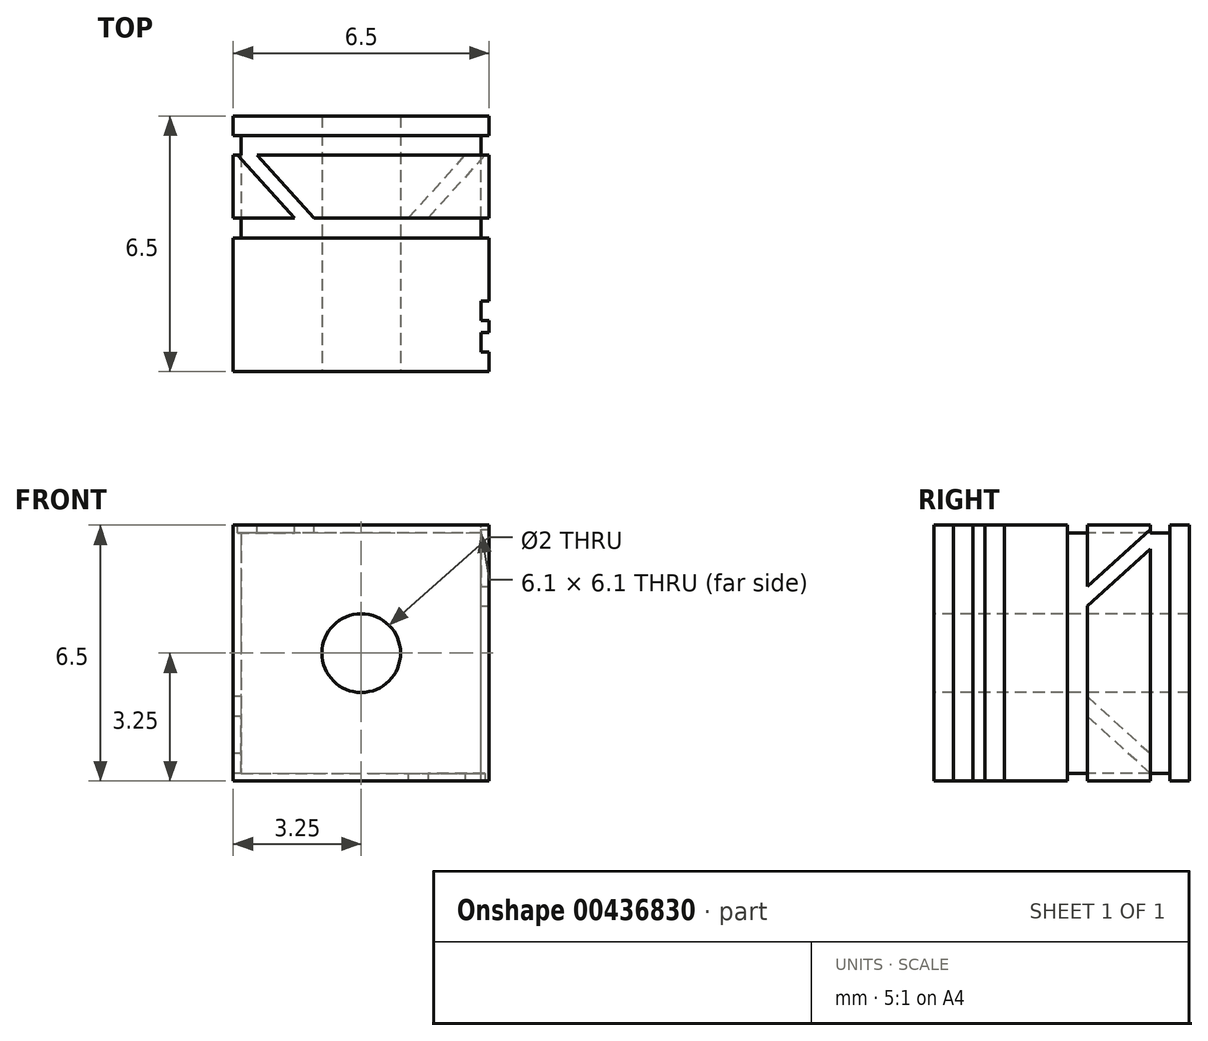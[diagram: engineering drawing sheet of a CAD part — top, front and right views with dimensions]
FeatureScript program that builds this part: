
annotation { "Feature Type Name" : "Feature", "Feature Type Description" : "" }
export const myFeature = defineFeature(function(context is Context, id is Id, definition is map)
    precondition{}
    {
        {
            var Q0;
            Q0=qCreatedBy(makeId("Front.planeOp"),FACE);
            var sketch = newSketch(context, id + "F0", { "sketchPlane" : qUnion([Q0])});
            skLineSegment(sketch, "E0.bottom", {"start": v(0, 0) * mm, "end": v(6.5, 0) * mm});
            skLineSegment(sketch, "E0.top", {"start": v(0, -6.5) * mm, "end": v(6.5, -6.5) * mm});
            skLineSegment(sketch, "E0.left", {"start": v(0, 0) * mm, "end": v(0, -6.5) * mm});
            skLineSegment(sketch, "E0.right", {"start": v(6.5, 0) * mm, "end": v(6.5, -6.5) * mm});
            skSolve(sketch);
        }
        {
            var Q0;
            Q0=makeQuery(id+"F0.imprint","IMPRINT",FACE,{"disambiguationData":[TD([[makeQuery(id+"F0.imprint","IMPRINT",EDGE,{"derivedFrom":sQuery(id+"F0.wireOp",EDGE,"E0.bottom")}),-1.0]])]});
            extrude(context, id + "F1", {"entities" : qUnion([Q0]), "depth" : 6.5 * mm});
        }
        {
            var Q0;
            Q0=makeQuery(id+"F1.opExtrude","CAP_FACE",FACE,{"disambiguationData":[OSD([sQuery(id+"F0.wireOp",EDGE,"E0.bottom"),sQuery(id+"F0.wireOp",EDGE,"E0.top"),sQuery(id+"F0.wireOp",EDGE,"E0.left"),sQuery(id+"F0.wireOp",EDGE,"E0.right")])],"isStart":false});
            var sketch = newSketch(context, id + "F2", { "sketchPlane" : qUnion([Q0])});
            skCircle(sketch, "E1", {"center": v(3.25, -3.25) * mm, "radius": 1 * mm});
            skPoint(sketch, "E1.centerSnap0", {"position": v(3.25, -6.5) * mm});
            skPoint(sketch, "E1.centerSnap1", {"position": v(0, -3.25) * mm});
            skLineSegment(sketch, "E2", {"start": v(0.3, 0) * mm, "end": v(0.3, -6.5) * mm});
            skLineSegment(sketch, "E3", {"start": v(0.45, -6.5) * mm, "end": v(0.45, 0) * mm});
            skSolve(sketch);
        }
        {
            var Q0;
            Q0=makeQuery(id+"F2.imprint","IMPRINT",FACE,{"disambiguationData":[TD([[makeQuery(id+"F2.imprint","IMPRINT",EDGE,{"derivedFrom":sQuery(id+"F2.wireOp",EDGE,"E1")}),1.0]])]});
            extrude(context, id + "F3", {"entities" : qUnion([Q0]), "operationType" : NewBodyOperationType.REMOVE, "oppositeDirection" : true, "depth" : 25 * mm});
        }
        {
            var Q0;
            Q0=makeQuery(id+"F1.opExtrude","SWEPT_FACE",FACE,{"disambiguationData":[OSD([sQuery(id+"F0.wireOp",EDGE,"E0.right")])]});
            var sketch = newSketch(context, id + "F4", { "sketchPlane" : qUnion([Q0])});
            skLineSegment(sketch, "E4", {"start": v(-6, -6.5) * mm, "end": v(-6, 0) * mm});
            skLineSegment(sketch, "E5", {"start": v(-0.5, -6.5) * mm, "end": v(-0.5, 0) * mm});
            skLineSegment(sketch, "E6.bottom", {"start": v(-5.5, -6.5) * mm, "end": v(-5.2, -6.5) * mm});
            skLineSegment(sketch, "E6.top", {"start": v(-5.5, 0) * mm, "end": v(-5.2, 0) * mm});
            skLineSegment(sketch, "E6.left", {"start": v(-5.5, -6.5) * mm, "end": v(-5.5, 0) * mm});
            skLineSegment(sketch, "E6.right", {"start": v(-5.2, -6.5) * mm, "end": v(-5.2, 0) * mm});
            skLineSegment(sketch, "E7.bottom", {"start": v(-4.7, -6.5) * mm, "end": v(-3.1, -6.5) * mm});
            skLineSegment(sketch, "E7.top", {"start": v(-4.7, 0) * mm, "end": v(-3.1, 0) * mm});
            skLineSegment(sketch, "E7.left", {"start": v(-4.7, -6.5) * mm, "end": v(-4.7, 0) * mm});
            skLineSegment(sketch, "E7.right", {"start": v(-3.1, -6.5) * mm, "end": v(-3.1, 0) * mm});
            skLineSegment(sketch, "E8.bottom", {"start": v(-2.6, -6.5) * mm, "end": v(-1, -6.5) * mm});
            skLineSegment(sketch, "E8.top", {"start": v(-2.6, 0) * mm, "end": v(-1, 0) * mm});
            skLineSegment(sketch, "E8.left", {"start": v(-2.6, -6.5) * mm, "end": v(-2.6, -2.06) * mm});
            skLineSegment(sketch, "E8.right", {"start": v(-1, -6.5) * mm, "end": v(-1, -0.6) * mm});
            skLineSegment(sketch, "E9", {"start": v(-1, -0.1) * mm, "end": v(-2.6, -1.56) * mm});
            skLineSegment(sketch, "E10", {"start": v(-2.6, -2.06) * mm, "end": v(-1, -0.6) * mm});
            skLineSegment(sketch, "E11.trimOffspring", {"start": v(-2.6, -1.56) * mm, "end": v(-2.6, 0) * mm});
            skLineSegment(sketch, "E12.trimOffspring", {"start": v(-1, -0.1) * mm, "end": v(-1, 0) * mm});
            skSolve(sketch);
        }
        {
            var Q0;
            {var subQ0=sQuery(id+"F4.wireOp",EDGE,"E4");Q0=makeQuery(id+"F4.imprint","IMPRINT",FACE,{"disambiguationData":[TD([[makeQuery(id+"F4.imprint","IMPRINT",EDGE,{"derivedFrom":subQ0}),-1.0]])]});}
            var Q1;
            {var subQ0=sQuery(id+"F4.wireOp",EDGE,"E6.right");Q1=makeQuery(id+"F4.imprint","IMPRINT",FACE,{"disambiguationData":[TD([[makeQuery(id+"F4.imprint","IMPRINT",EDGE,{"derivedFrom":subQ0}),-1.0]])]});}
            var Q2;
            {var subQ6=sQuery(id+"F4.wireOp",EDGE,"E5");Q2=makeQuery(id+"F4.imprint","IMPRINT",FACE,{"disambiguationData":[TD([[makeQuery(id+"F4.imprint","IMPRINT",EDGE,{"derivedFrom":subQ6}),1.0]])]});}
            extrude(context, id + "F5", {"entities" : qUnion([Q0, Q1, Q2]), "operationType" : NewBodyOperationType.REMOVE, "oppositeDirection" : true, "depth" : 0.2 * mm});
        }
        {
            var Q0;
            Q0=makeQuery(id+"F1.opExtrude","SWEPT_FACE",FACE,{"disambiguationData":[OSD([sQuery(id+"F0.wireOp",EDGE,"E0.bottom")])]});
            var sketch = newSketch(context, id + "F6", { "sketchPlane" : qUnion([Q0])});
            skLineSegment(sketch, "E13", {"start": v(6.5, -6) * mm, "end": v(0, -6) * mm});
            skLineSegment(sketch, "E14", {"start": v(6.5, -0.5) * mm, "end": v(0, -0.5) * mm});
            skLineSegment(sketch, "E15.bottom", {"start": v(6.5, -5.5) * mm, "end": v(6.5, -5.2) * mm});
            skLineSegment(sketch, "E15.top", {"start": v(0, -5.5) * mm, "end": v(0, -5.2) * mm});
            skLineSegment(sketch, "E15.left", {"start": v(6.5, -5.5) * mm, "end": v(0, -5.5) * mm});
            skLineSegment(sketch, "E15.right", {"start": v(6.5, -5.2) * mm, "end": v(0, -5.2) * mm});
            skLineSegment(sketch, "E16.bottom", {"start": v(6.5, -4.7) * mm, "end": v(6.5, -3.1) * mm});
            skLineSegment(sketch, "E16.top", {"start": v(0, -4.7) * mm, "end": v(0, -3.1) * mm});
            skLineSegment(sketch, "E16.left", {"start": v(6.5, -4.7) * mm, "end": v(0, -4.7) * mm});
            skLineSegment(sketch, "E16.right", {"start": v(6.5, -3.1) * mm, "end": v(0, -3.1) * mm});
            skLineSegment(sketch, "E17.bottom", {"start": v(6.5, -2.6) * mm, "end": v(6.5, -1) * mm});
            skLineSegment(sketch, "E17.top", {"start": v(0, -2.6) * mm, "end": v(0, -1) * mm});
            skLineSegment(sketch, "E17.left", {"start": v(6.5, -2.6) * mm, "end": v(2.06, -2.6) * mm});
            skLineSegment(sketch, "E17.right", {"start": v(6.5, -1) * mm, "end": v(0.6, -1) * mm});
            skLineSegment(sketch, "E18", {"start": v(0.1, -1) * mm, "end": v(1.56, -2.6) * mm});
            skLineSegment(sketch, "E19", {"start": v(2.06, -2.6) * mm, "end": v(0.6, -1) * mm});
            skLineSegment(sketch, "E20.trimOffspring", {"start": v(1.56, -2.6) * mm, "end": v(0, -2.6) * mm});
            skLineSegment(sketch, "E21.trimOffspring", {"start": v(0.1, -1) * mm, "end": v(0, -1) * mm});
            skSolve(sketch);
        }
        {
            var Q0;
            {var subQ1=sQuery(id+"F0.wireOp",EDGE,"E0.right");var subQ2=sQuery(id+"F0.wireOp",EDGE,"E0.bottom");var subQ3=makeQuery(id+"F1.opExtrude","SWEPT_EDGE",EDGE,{"disambiguationData":[OSD([subQ2,subQ1])]});var subQ4=makeQuery(id+"F5.boolean.opBoolean","COPY",EDGE,{"derivedFrom":makeQuery(id+"F5.opExtrude","CAP_EDGE",EDGE,{"disambiguationData":[OSD([subQ2,subQ1]),TDD([makeQuery(id+"F4.imprint","IMPRINT",EDGE,{"disambiguationData":[TD([[makeQuery(id+"F4.imprint","INTERSECT",VERTEX,{"derivedFrom":[subQ3,sQuery(id+"F4.wireOp",EDGE,"E4")]}),-1.0]])],"derivedFrom":subQ3})])],"isStart":false})});Q0=makeQuery(id+"F6.imprint","IMPRINT",FACE,{"disambiguationData":[TD([[makeQuery(id+"F6.imprint","IMPRINT",EDGE,{"derivedFrom":subQ4}),1.0]])]});}
            var Q1;
            {var subQ1=sQuery(id+"F0.wireOp",EDGE,"E0.right");var subQ2=sQuery(id+"F0.wireOp",EDGE,"E0.bottom");var subQ3=makeQuery(id+"F1.opExtrude","SWEPT_EDGE",EDGE,{"disambiguationData":[OSD([subQ2,subQ1])]});var subQ4=makeQuery(id+"F5.boolean.opBoolean","COPY",EDGE,{"derivedFrom":makeQuery(id+"F5.opExtrude","CAP_EDGE",EDGE,{"disambiguationData":[OSD([subQ2,subQ1]),TDD([makeQuery(id+"F4.imprint","IMPRINT",EDGE,{"disambiguationData":[TD([[makeQuery(id+"F4.imprint","INTERSECT",VERTEX,{"derivedFrom":[subQ3,sQuery(id+"F4.wireOp",EDGE,"E6.top"),sQuery(id+"F4.wireOp",EDGE,"E6.right")]}),-1.0]])],"derivedFrom":subQ3})])],"isStart":false})});Q1=makeQuery(id+"F6.imprint","IMPRINT",FACE,{"disambiguationData":[TD([[makeQuery(id+"F6.imprint","IMPRINT",EDGE,{"derivedFrom":subQ4}),1.0]])]});}
            var Q2;
            Q2=makeQuery(id+"F6.imprint","IMPRINT",FACE,{"disambiguationData":[TD([[makeQuery(id+"F6.imprint","IMPRINT",EDGE,{"derivedFrom":sQuery(id+"F6.wireOp",EDGE,"E18")}),1.0]])]});
            extrude(context, id + "F7", {"entities" : qUnion([Q0, Q1, Q2]), "operationType" : NewBodyOperationType.REMOVE, "oppositeDirection" : true, "depth" : 0.2 * mm});
        }
        {
            var Q0;
            Q0=makeQuery(id+"F1.opExtrude","SWEPT_FACE",FACE,{"disambiguationData":[OSD([sQuery(id+"F0.wireOp",EDGE,"E0.left")])]});
            var sketch = newSketch(context, id + "F8", { "sketchPlane" : qUnion([Q0])});
            skLineSegment(sketch, "E22", {"start": v(6, 0) * mm, "end": v(6, -6.5) * mm});
            skLineSegment(sketch, "E23", {"start": v(0.5, 0) * mm, "end": v(0.5, -6.5) * mm});
            skLineSegment(sketch, "E24.bottom", {"start": v(5.5, 0) * mm, "end": v(5.2, 0) * mm});
            skLineSegment(sketch, "E24.top", {"start": v(5.5, -6.5) * mm, "end": v(5.2, -6.5) * mm});
            skLineSegment(sketch, "E24.left", {"start": v(5.5, 0) * mm, "end": v(5.5, -6.5) * mm});
            skLineSegment(sketch, "E24.right", {"start": v(5.2, 0) * mm, "end": v(5.2, -6.5) * mm});
            skLineSegment(sketch, "E25.bottom", {"start": v(4.7, 0) * mm, "end": v(3.1, 0) * mm});
            skLineSegment(sketch, "E25.top", {"start": v(4.7, -6.5) * mm, "end": v(3.1, -6.5) * mm});
            skLineSegment(sketch, "E25.left", {"start": v(4.7, 0) * mm, "end": v(4.7, -6.5) * mm});
            skLineSegment(sketch, "E25.right", {"start": v(3.1, 0) * mm, "end": v(3.1, -6.5) * mm});
            skLineSegment(sketch, "E26.bottom", {"start": v(2.6, 0) * mm, "end": v(1, 0) * mm});
            skLineSegment(sketch, "E26.top", {"start": v(2.6, -6.5) * mm, "end": v(1, -6.5) * mm});
            skLineSegment(sketch, "E26.left", {"start": v(2.6, 0) * mm, "end": v(2.6, -4.35) * mm});
            skLineSegment(sketch, "E26.right", {"start": v(1, 0) * mm, "end": v(1, -5.8) * mm});
            skLineSegment(sketch, "E27", {"start": v(1, -6.3) * mm, "end": v(2.6, -4.85) * mm});
            skLineSegment(sketch, "E28", {"start": v(2.6, -4.35) * mm, "end": v(1, -5.8) * mm});
            skLineSegment(sketch, "E29.trimOffspring", {"start": v(2.6, -4.85) * mm, "end": v(2.6, -6.5) * mm});
            skLineSegment(sketch, "E30.trimOffspring", {"start": v(1, -6.3) * mm, "end": v(1, -6.5) * mm});
            skSolve(sketch);
        }
        {
            var Q0;
            {var subQ1=sQuery(id+"F0.wireOp",EDGE,"E0.left");var subQ2=sQuery(id+"F0.wireOp",EDGE,"E0.bottom");var subQ3=makeQuery(id+"F1.opExtrude","SWEPT_EDGE",EDGE,{"disambiguationData":[OSD([subQ2,subQ1])]});var subQ4=makeQuery(id+"F7.boolean.opBoolean","COPY",EDGE,{"derivedFrom":makeQuery(id+"F7.opExtrude","CAP_EDGE",EDGE,{"disambiguationData":[OSD([subQ2,subQ1]),TDD([makeQuery(id+"F6.imprint","IMPRINT",EDGE,{"disambiguationData":[TD([[makeQuery(id+"F6.imprint","INTERSECT",VERTEX,{"derivedFrom":[subQ3,sQuery(id+"F6.wireOp",EDGE,"E13")]}),-1.0]])],"derivedFrom":subQ3})])],"isStart":false})});Q0=makeQuery(id+"F8.imprint","IMPRINT",FACE,{"disambiguationData":[TD([[makeQuery(id+"F8.imprint","IMPRINT",EDGE,{"derivedFrom":subQ4}),1.0]])]});}
            var Q1;
            {var subQ1=sQuery(id+"F0.wireOp",EDGE,"E0.left");var subQ2=sQuery(id+"F0.wireOp",EDGE,"E0.bottom");var subQ3=makeQuery(id+"F1.opExtrude","SWEPT_EDGE",EDGE,{"disambiguationData":[OSD([subQ2,subQ1])]});var subQ4=makeQuery(id+"F7.boolean.opBoolean","COPY",EDGE,{"derivedFrom":makeQuery(id+"F7.opExtrude","CAP_EDGE",EDGE,{"disambiguationData":[OSD([subQ2,subQ1]),TDD([makeQuery(id+"F6.imprint","IMPRINT",EDGE,{"disambiguationData":[TD([[makeQuery(id+"F6.imprint","INTERSECT",VERTEX,{"derivedFrom":[subQ3,sQuery(id+"F6.wireOp",EDGE,"E15.top"),sQuery(id+"F6.wireOp",EDGE,"E15.right")]}),-1.0]])],"derivedFrom":subQ3})])],"isStart":false})});Q1=makeQuery(id+"F8.imprint","IMPRINT",FACE,{"disambiguationData":[TD([[makeQuery(id+"F8.imprint","IMPRINT",EDGE,{"derivedFrom":subQ4}),1.0]])]});}
            var Q2;
            Q2=makeQuery(id+"F8.imprint","IMPRINT",FACE,{"disambiguationData":[TD([[makeQuery(id+"F8.imprint","IMPRINT",EDGE,{"derivedFrom":sQuery(id+"F8.wireOp",EDGE,"E27")}),1.0]])]});
            extrude(context, id + "F9", {"entities" : qUnion([Q0, Q1, Q2]), "operationType" : NewBodyOperationType.REMOVE, "oppositeDirection" : true, "depth" : 0.2 * mm});
        }
        {
            var Q0;
            Q0=makeQuery(id+"F1.opExtrude","SWEPT_FACE",FACE,{"disambiguationData":[OSD([sQuery(id+"F0.wireOp",EDGE,"E0.top")])]});
            var sketch = newSketch(context, id + "F10", { "sketchPlane" : qUnion([Q0])});
            skLineSegment(sketch, "E31", {"start": v(0, 6) * mm, "end": v(6.5, 6) * mm});
            skLineSegment(sketch, "E32", {"start": v(0, 0.5) * mm, "end": v(6.5, 0.5) * mm});
            skLineSegment(sketch, "E33.bottom", {"start": v(0, 5.5) * mm, "end": v(0, 5.2) * mm});
            skLineSegment(sketch, "E33.top", {"start": v(6.5, 5.5) * mm, "end": v(6.5, 5.2) * mm});
            skLineSegment(sketch, "E33.left", {"start": v(0, 5.5) * mm, "end": v(6.5, 5.5) * mm});
            skLineSegment(sketch, "E33.right", {"start": v(0, 5.2) * mm, "end": v(6.5, 5.2) * mm});
            skLineSegment(sketch, "E34.bottom", {"start": v(0, 4.7) * mm, "end": v(0, 3.1) * mm});
            skLineSegment(sketch, "E34.top", {"start": v(6.5, 4.7) * mm, "end": v(6.5, 3.1) * mm});
            skLineSegment(sketch, "E34.left", {"start": v(0, 4.7) * mm, "end": v(6.5, 4.7) * mm});
            skLineSegment(sketch, "E34.right", {"start": v(0, 3.1) * mm, "end": v(6.5, 3.1) * mm});
            skLineSegment(sketch, "E35.bottom", {"start": v(0, 2.6) * mm, "end": v(0, 1) * mm});
            skLineSegment(sketch, "E35.top", {"start": v(6.5, 2.6) * mm, "end": v(6.5, 1) * mm});
            skLineSegment(sketch, "E35.left", {"start": v(0, 2.6) * mm, "end": v(4.44, 2.6) * mm});
            skLineSegment(sketch, "E35.right", {"start": v(0, 1) * mm, "end": v(5.9, 1) * mm});
            skLineSegment(sketch, "E36", {"start": v(6.4, 1) * mm, "end": v(4.94, 2.6) * mm});
            skLineSegment(sketch, "E37", {"start": v(4.44, 2.6) * mm, "end": v(5.9, 1) * mm});
            skLineSegment(sketch, "E38.trimOffspring", {"start": v(4.94, 2.6) * mm, "end": v(6.5, 2.6) * mm});
            skLineSegment(sketch, "E39.trimOffspring", {"start": v(6.4, 1) * mm, "end": v(6.5, 1) * mm});
            skSolve(sketch);
        }
        {
            var Q0;
            {var subQ1=sQuery(id+"F0.wireOp",EDGE,"E0.right");var subQ2=sQuery(id+"F0.wireOp",EDGE,"E0.top");var subQ3=makeQuery(id+"F1.opExtrude","SWEPT_EDGE",EDGE,{"disambiguationData":[OSD([subQ2,subQ1])]});var subQ4=makeQuery(id+"F5.boolean.opBoolean","COPY",EDGE,{"derivedFrom":makeQuery(id+"F5.opExtrude","CAP_EDGE",EDGE,{"disambiguationData":[OSD([subQ2,subQ1]),TDD([makeQuery(id+"F4.imprint","IMPRINT",EDGE,{"disambiguationData":[TD([[makeQuery(id+"F4.imprint","INTERSECT",VERTEX,{"derivedFrom":[subQ3,sQuery(id+"F4.wireOp",EDGE,"E4")]}),-1.0]])],"derivedFrom":subQ3})])],"isStart":false})});Q0=makeQuery(id+"F10.imprint","IMPRINT",FACE,{"disambiguationData":[TD([[makeQuery(id+"F10.imprint","IMPRINT",EDGE,{"derivedFrom":subQ4}),-1.0]])]});}
            var Q1;
            {var subQ1=sQuery(id+"F0.wireOp",EDGE,"E0.right");var subQ2=sQuery(id+"F0.wireOp",EDGE,"E0.top");var subQ3=makeQuery(id+"F1.opExtrude","SWEPT_EDGE",EDGE,{"disambiguationData":[OSD([subQ2,subQ1])]});var subQ4=makeQuery(id+"F5.boolean.opBoolean","COPY",EDGE,{"derivedFrom":makeQuery(id+"F5.opExtrude","CAP_EDGE",EDGE,{"disambiguationData":[OSD([subQ2,subQ1]),TDD([makeQuery(id+"F4.imprint","IMPRINT",EDGE,{"disambiguationData":[TD([[makeQuery(id+"F4.imprint","INTERSECT",VERTEX,{"derivedFrom":[subQ3,sQuery(id+"F4.wireOp",EDGE,"E6.bottom"),sQuery(id+"F4.wireOp",EDGE,"E6.right")]}),-1.0]])],"derivedFrom":subQ3})])],"isStart":false})});Q1=makeQuery(id+"F10.imprint","IMPRINT",FACE,{"disambiguationData":[TD([[makeQuery(id+"F10.imprint","IMPRINT",EDGE,{"derivedFrom":subQ4}),-1.0]])]});}
            var Q2;
            {var subQ6=sQuery(id+"F10.wireOp",EDGE,"E36");Q2=makeQuery(id+"F10.imprint","IMPRINT",FACE,{"disambiguationData":[TD([[makeQuery(id+"F10.imprint","IMPRINT",EDGE,{"derivedFrom":subQ6}),1.0]])]});}
            extrude(context, id + "F11", {"entities" : qUnion([Q0, Q1, Q2]), "operationType" : NewBodyOperationType.REMOVE, "oppositeDirection" : true, "depth" : 0.2 * mm});
        }
    });
